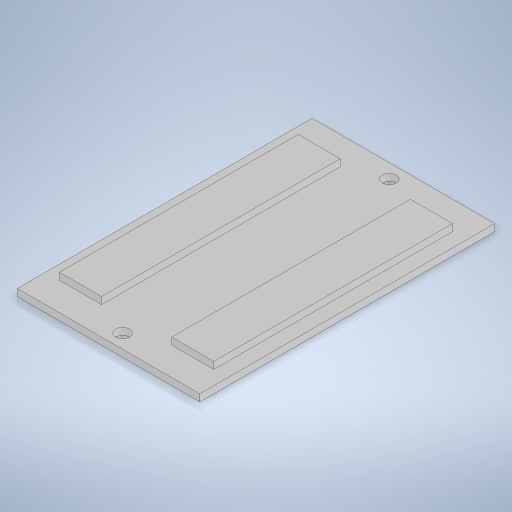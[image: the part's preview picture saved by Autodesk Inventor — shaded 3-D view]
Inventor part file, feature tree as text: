
AUTODESK INVENTOR PART (.ipt)
format: ipt  version: 2024 (Build 280153000, 153)  size: 256,512 bytes
history: native  units: mm
features: sketch x4, extrude x3, hole x1, projected_geometry x1
ambient origin geometry x8: Origin, YZ Plane, XZ Plane, XY Plane, X Axis, Y Axis, Z Axis, Center Point
bodies: Volumenkörper1 (feature_tree)
feature tree (9):
  extrude  "Extrusion1"  Depth=84.0mm
  extrude  "Extrusion2"  Depth=4.0mm
  extrude  "Extrusion3"  Depth=8.0mm
  hole  "Bohrung1"  [1 undecoded]
  sketch  "Skizze1"  dims[d0=52.0mm d1=84.0mm]
  sketch  "Skizze2"  dims[d2=2.0mm d3=0.0mm d4=4.0mm]
  sketch  "Skizze3"  dims[d5=8.0mm d6=8.0mm]
  projected_geometry  "Projizierte Kontur1"
  sketch  "Skizze4"  dims[d7=2.0mm d8=0.0mm d9=20.0mm d10=12.0mm d11=0.0mm d12=0.0mm d13=4.0mm d14=6.0mm d15=4.0mm d16=2.0mm d17=90.0deg d18=8.0mm d19=0.0mm d20=4.0mm d21=4.0mm]
note: 1 required parameter value undecoded (feature->parameter linkage not recoverable at this tier; creation-order binding heuristic only, values carry confidence <= 0.55)
